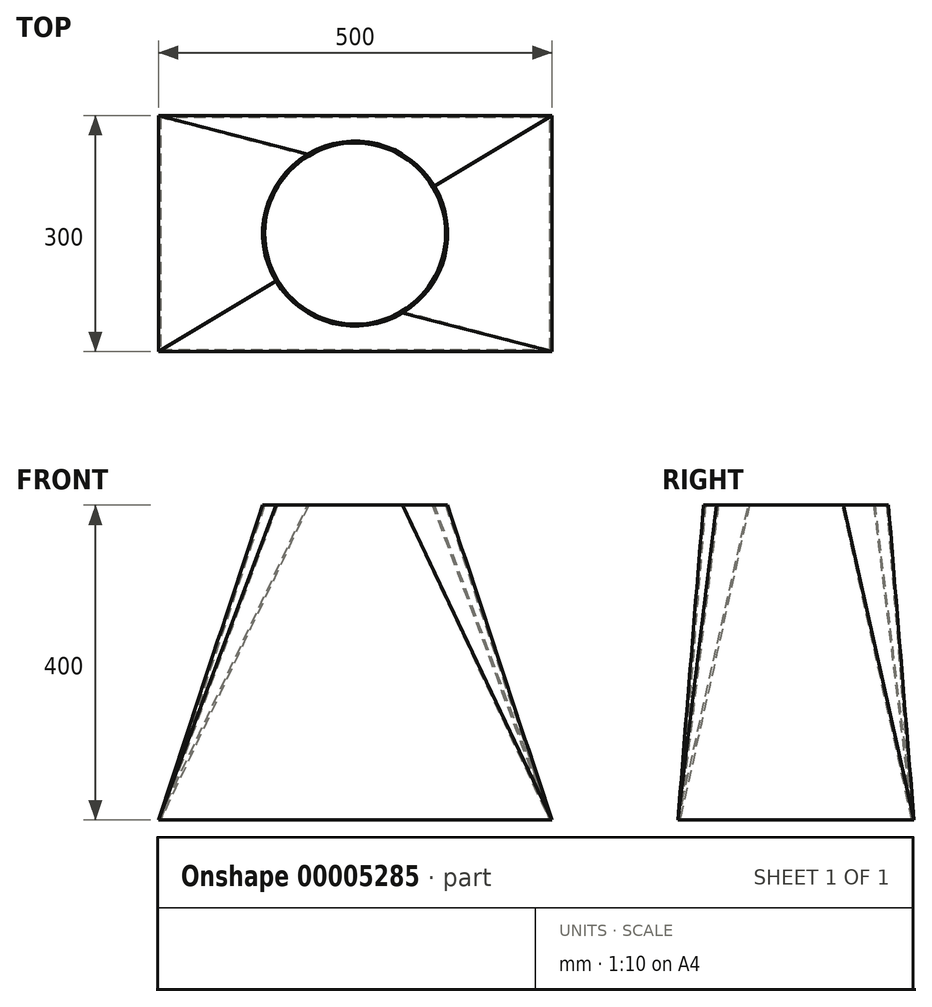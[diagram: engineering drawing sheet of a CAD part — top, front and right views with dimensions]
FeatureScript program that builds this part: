
annotation { "Feature Type Name" : "Feature", "Feature Type Description" : "" }
export const myFeature = defineFeature(function(context is Context, id is Id, definition is map)
    precondition{}
    {
        {
            var Q0;
            Q0=qCreatedBy(makeId("Top.planeOp"),FACE);
            var sketch = newSketch(context, id + "F0", { "sketchPlane" : qUnion([Q0])});
            skLineSegment(sketch, "E0.rect.bottom", {"start": v(250, 150) * mm, "end": v(-250, 150) * mm});
            skLineSegment(sketch, "E0.rect.top", {"start": v(250, -150) * mm, "end": v(-250, -150) * mm});
            skLineSegment(sketch, "E0.rect.left", {"start": v(250, 150) * mm, "end": v(250, -150) * mm});
            skLineSegment(sketch, "E0.rect.right", {"start": v(-250, 150) * mm, "end": v(-250, -150) * mm});
            skPoint(sketch, "E0.rect.middle", {"position": v(0, 0) * mm});
            skSolve(sketch);
        }
        {
            var Q0;
            Q0=makeQuery(id+"F0.imprint","IMPRINT",FACE,{"disambiguationData":[TD([[makeQuery(id+"F0.imprint","IMPRINT",EDGE,{"derivedFrom":sQuery(id+"F0.wireOp",EDGE,"E0.rect.bottom")}),1.0]])]});
            cPlane(context, id + "F1", {"entities" : qUnion([Q0]), "cplaneType" : CPlaneType.OFFSET, "offset" : 400 * mm, "width" : 150 * mm, "height" : 150 * mm});
        }
        {
            var Q0;
            Q0=qCreatedBy(id+"F1.planeOp",FACE);
            var sketch = newSketch(context, id + "F2", { "sketchPlane" : qUnion([Q0])});
            skCircle(sketch, "E1", {"center": v(0, 0) * mm, "radius": 117.5 * mm});
            skSolve(sketch);
        }
        {
            var Q0;
            Q0=makeQuery(id+"F0.imprint","IMPRINT",FACE,{"disambiguationData":[TD([[makeQuery(id+"F0.imprint","IMPRINT",EDGE,{"derivedFrom":sQuery(id+"F0.wireOp",EDGE,"E0.rect.bottom")}),1.0]])]});
            var Q1;
            Q1=makeQuery(id+"F2.imprint","IMPRINT",FACE,{"disambiguationData":[TD([[makeQuery(id+"F2.imprint","IMPRINT",EDGE,{"derivedFrom":sQuery(id+"F2.wireOp",EDGE,"E1")}),1.0]])]});
            loft(context, id + "F3", {"sheetProfilesArray" : [{ "sheetProfileEntities" : qUnion([Q0]) }, { "sheetProfileEntities" : qUnion([Q1]) }]});
        }
        {
            var Q0;
            Q0=makeQuery(id+"F3.opLoft","CAP_FACE",FACE,{"disambiguationData":[OSD([makeQuery(id+"F2.imprint","IMPRINT",FACE,{"disambiguationData":[TD([[makeQuery(id+"F2.imprint","IMPRINT",EDGE,{"derivedFrom":sQuery(id+"F2.wireOp",EDGE,"E1")}),1.0]])]})])],"isStart":true});
            var Q1;
            Q1=makeQuery(id+"F3.opLoft","CAP_FACE",FACE,{"disambiguationData":[OSD([makeQuery(id+"F0.imprint","IMPRINT",FACE,{"disambiguationData":[TD([[makeQuery(id+"F0.imprint","IMPRINT",EDGE,{"derivedFrom":sQuery(id+"F0.wireOp",EDGE,"E0.rect.bottom")}),1.0]])]})])],"isStart":true});
            shell(context, id + "F4", {"entities" : qUnion([Q0, Q1]), "thickness" : 2.5 * mm});
        }
    });
